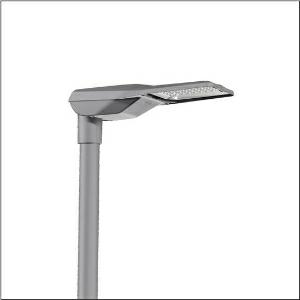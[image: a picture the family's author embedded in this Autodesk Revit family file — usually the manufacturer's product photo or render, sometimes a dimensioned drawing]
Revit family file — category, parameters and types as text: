
# Revit family: streetlight_sl_21_mini___stw1_0a_5xe6e43a08hb_5b98
name_source: partatom
category: Lighting Fixtures
units: mm (PartAtom-declared; Revit-internal decimal feet)

## family parameters
Cut with Voids When Loaded = No
Host = Face
Light Source = No
Part Type = Normal
Room Calculation Point = No
Round Connector Dimension = Use Diameter
Shared = No

## types (1)
- --- (1 x LED, 9430 lm, 66 W, 4000K)
    Apparent Load = 66 VA
    CIE Flux Codes = 38 75 98 100 100
    Color Rendering = 70
    Color Temperature = 4000K
    Default Elevation = 1800 mm
    Description = Streetlight SL 21 mini, mast luminaire, primary light control with lens, of PMMA, primary optical cover: cover, of toughened safety glass, transparent, light distribution: STW1.0a, light emission: direct distribution, primary light characteristic: asymmetric, installation type: post-top, side-entry, LED, 3G 1.5mm², High Power LED, rated luminous flux: 9.430lm, luminous efficacy: 143lm/W, light colour: 740, colour temperature: 4000K, control gear: Easy, control: overheat protection, constant luminous flux control, time-dependent luminous flux control, flexible luminous flux parameterisation, mains connection: 230..240V, AC, 50/60Hz, connection cable pre-assembled, cable length: 8,5m, wiring characteristics: H07RN-F, start of lifetime: 66W, end of service life: 69W, reduction: 30W, luminaire housing, of diecast aluminium, powder-coated, Siteco® metallic grey (DB 702S), corrosivity category C5 mid according to DIN EN ISO 12944, please order mast flange separately, inclination adjustable: 0°, 5°, 10°, 15°, sealing non-destructively replaceable, multi-level sealing system, length: 628mm, width: 235mm, height: 110mm, mast flange for spigot size: 42mm (side-entry): 5XC10008XM4, 60/48mm (side-entry/post-top): 5XC10108XM2, 76/60mm (side-entry/post-top): 5XC10108XM1, mounting height: 4..8m, protection rating (complete): IP66, insulation class (complete): insulation class II (safety insulation), certification: CE, ENEC, ENEC+, VDE, impact resistance: IK10, permissible operating ambient temperature for outdoor applications: -40..+50°C, standard-compliant lighting for roads and squares, packaging unit: 1 piece

Light Distribution: STW1.0a
    Height = 110 mm
    Lamp = 1 x LED
    Lamp Light Flux = 9430 lm
    Lamp Power = 66 W
    Lamp count = 1
    Length = 625 mm
    Luminous efficacy = 143 lm/W
    Manufacturer = Siteco
    ModVariant = No
    Model = 5XE6E43A08HB
    Number of Poles = 1
    OnlyDefault = Yes
    Power Factor = 1
    Product Name = Streetlight SL 21 mini | STW1.0a
    Product group = mast luminaire | pylon top
    ProductGroupID = 6100
    Protection Class = Protection class II
    Protection Degree = IP 66
    RLX_Detail_Level = 1
    RLX_Emergency_Light_Flux = 0 lm
    RLX_Emergency_Type = 0
    RLX_Emergency_Type_DB = No
    RlxData = <blob elided: 26185 chars, md5=e64eb701>
    Socket = socket
    Standby Power = 0 W
    System Light Flux = 9430 lm
    System Power = 66 W
    Type Comments = factory setting: luminous flux: 100 % | Output Level: 100 % | 670 mA
    Type Image = l_1003519.jpg
    URL = http://relux.com
    VarID = @adj_208229
    Voltage = 0 V
    Weight = 0.00 kg
    Width = 234 mm

## geometry (parser evidence)
native form markers: Blend x4, Sweep x11
no freeform markers — native parametric forms only
